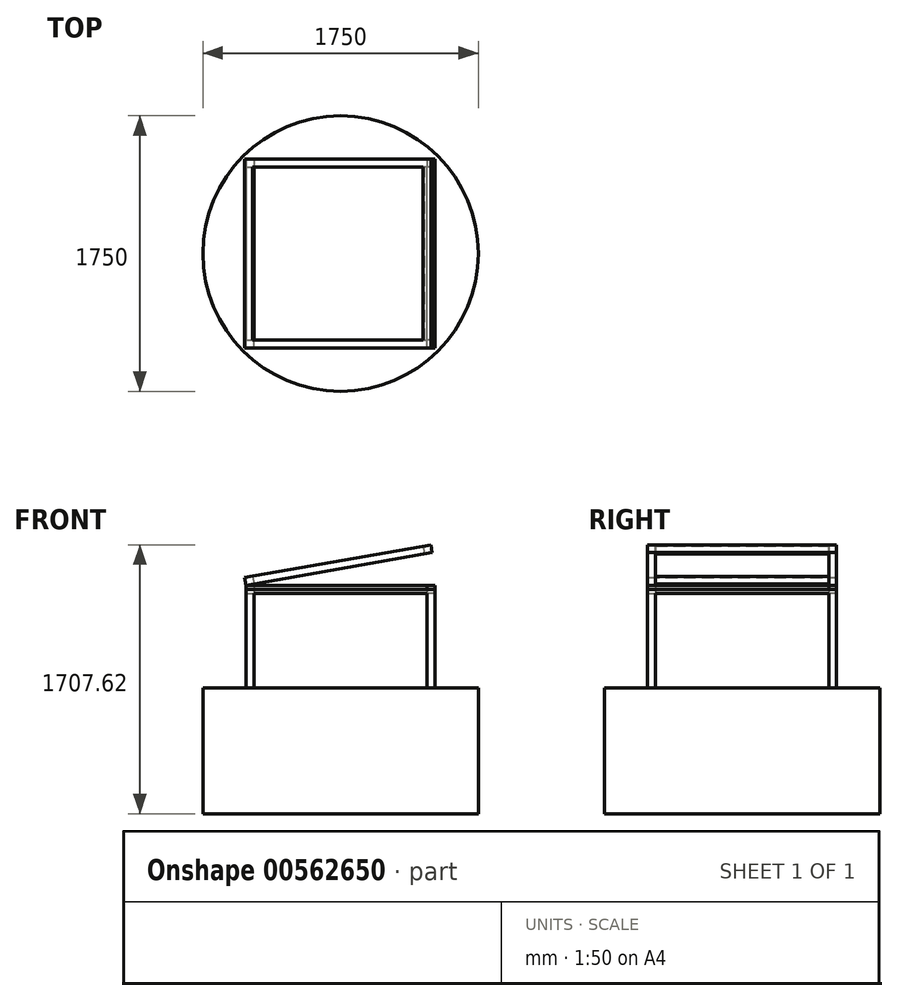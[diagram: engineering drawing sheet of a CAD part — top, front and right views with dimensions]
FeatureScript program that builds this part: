
annotation { "Feature Type Name" : "Feature", "Feature Type Description" : "" }
export const myFeature = defineFeature(function(context is Context, id is Id, definition is map)
    precondition{}
    {
        {
            var Q0;
            Q0=qCreatedBy(makeId("Top.planeOp"),FACE);
            var sketch = newSketch(context, id + "F0", { "sketchPlane" : qUnion([Q0])});
            skCircle(sketch, "E0", {"center": v(0, 0) * mm, "radius": 875 * mm});
            skSolve(sketch);
        }
        {
            var Q0;
            Q0=qSketchRegion(id+"F0",true);
            extrude(context, id + "F1", {"entities" : qUnion([Q0]), "oppositeDirection" : true, "depth" : 800 * mm});
        }
        {
            var Q0;
            Q0=qCreatedBy(makeId("Top.planeOp"),FACE);
            cPlane(context, id + "F2", {"entities" : qUnion([Q0]), "cplaneType" : CPlaneType.OFFSET, "offset" : 600 * mm, "width" : 150 * mm, "height" : 150 * mm});
        }
        {
            var Q0;
            Q0=qCreatedBy(id+"F2.planeOp",FACE);
            var sketch = newSketch(context, id + "F3", { "sketchPlane" : qUnion([Q0])});
            skLineSegment(sketch, "E1.bottom", {"start": v(600, -550) * mm, "end": v(550, -550) * mm});
            skLineSegment(sketch, "E1.top", {"start": v(600, 600) * mm, "end": v(550, 600) * mm});
            skLineSegment(sketch, "E1.left", {"start": v(600, -550) * mm, "end": v(600, 600) * mm});
            skLineSegment(sketch, "E1.right", {"start": v(550, -550) * mm, "end": v(550, 600) * mm});
            skSolve(sketch);
        }
        {
            var Q0;
            Q0=makeQuery(id+"F3.imprint","IMPRINT",FACE,{"disambiguationData":[TD([[makeQuery(id+"F3.imprint","IMPRINT",EDGE,{"derivedFrom":sQuery(id+"F3.wireOp",EDGE,"E1.bottom")}),-1.0]])]});
            extrude(context, id + "F4", {"entities" : qUnion([Q0]), "depth" : 25 * mm});
        }
        {
            var Q0;
            Q0=makeQuery(id+"F4.opExtrude","SWEPT_BODY",BODY,{"disambiguationData":[OSD([sQuery(id+"F3.wireOp",EDGE,"E1.bottom"),sQuery(id+"F3.wireOp",EDGE,"E1.top"),sQuery(id+"F3.wireOp",EDGE,"E1.left"),sQuery(id+"F3.wireOp",EDGE,"E1.right")])]});
            var Q1;
            Q1=makeQuery(id+"F1.opExtrude","SWEPT_FACE",FACE,{"disambiguationData":[OSD([sQuery(id+"F0.wireOp",EDGE,"E0")])]});
            circularPattern(context, id + "F5", {"entities" : qUnion([Q0]), "axis" : qUnion([Q1]), "angle" : 90 * degree, "instanceCount" : 4, "computeTransformsWithoutBuiltin" : true});
        }
        {
            var Q0;
            Q0=makeQuery(id+"F4.opExtrude","CAP_FACE",FACE,{"disambiguationData":[OSD([sQuery(id+"F3.wireOp",EDGE,"E1.bottom"),sQuery(id+"F3.wireOp",EDGE,"E1.top"),sQuery(id+"F3.wireOp",EDGE,"E1.left"),sQuery(id+"F3.wireOp",EDGE,"E1.right")])],"isStart":false});
            var sketch = newSketch(context, id + "F6", { "sketchPlane" : qUnion([Q0])});
            skLineSegment(sketch, "E2.bottom", {"start": v(-600, -600) * mm, "end": v(550, -600) * mm});
            skLineSegment(sketch, "E2.top", {"start": v(-600, -550) * mm, "end": v(550, -550) * mm});
            skLineSegment(sketch, "E2.left", {"start": v(-600, -600) * mm, "end": v(-600, -550) * mm});
            skLineSegment(sketch, "E2.right", {"start": v(550, -600) * mm, "end": v(550, -550) * mm});
            skSolve(sketch);
        }
        {
            var Q0;
            Q0=qSketchRegion(id+"F6",true);
            extrude(context, id + "F7", {"entities" : qUnion([Q0]), "depth" : 25 * mm});
        }
        {
            var Q0;
            Q0=makeQuery(id+"F7.opExtrude","SWEPT_BODY",BODY,{"disambiguationData":[OSD([sQuery(id+"F6.wireOp",EDGE,"E2.bottom"),sQuery(id+"F6.wireOp",EDGE,"E2.top"),sQuery(id+"F6.wireOp",EDGE,"E2.left"),sQuery(id+"F6.wireOp",EDGE,"E2.right")])]});
            var Q1;
            Q1=makeQuery(id+"F1.opExtrude","SWEPT_FACE",FACE,{"disambiguationData":[OSD([sQuery(id+"F0.wireOp",EDGE,"E0")])]});
            circularPattern(context, id + "F8", {"entities" : qUnion([Q0]), "axis" : qUnion([Q1]), "angle" : 90 * degree, "instanceCount" : 4, "computeTransformsWithoutBuiltin" : true});
        }
        {
            var Q0;
            Q0=qCreatedBy(id+"F2.planeOp",FACE);
            var sketch = newSketch(context, id + "F9", { "sketchPlane" : qUnion([Q0])});
            skLineSegment(sketch, "E3.bottom", {"start": v(600, -600) * mm, "end": v(550, -600) * mm});
            skLineSegment(sketch, "E3.top", {"start": v(600, -550) * mm, "end": v(550, -550) * mm});
            skLineSegment(sketch, "E3.left", {"start": v(600, -600) * mm, "end": v(600, -550) * mm});
            skLineSegment(sketch, "E3.right", {"start": v(550, -600) * mm, "end": v(550, -550) * mm});
            skSolve(sketch);
        }
        {
            var Q0;
            Q0=qSketchRegion(id+"F9",true);
            extrude(context, id + "F10", {"entities" : qUnion([Q0]), "oppositeDirection" : true, "depth" : 800 * mm});
        }
        {
            var Q0;
            Q0=makeQuery(id+"F10.opExtrude","SWEPT_BODY",BODY,{"disambiguationData":[OSD([sQuery(id+"F9.wireOp",EDGE,"E3.bottom"),sQuery(id+"F9.wireOp",EDGE,"E3.top"),sQuery(id+"F9.wireOp",EDGE,"E3.left"),sQuery(id+"F9.wireOp",EDGE,"E3.right")])]});
            var Q1;
            Q1=makeQuery(id+"F1.opExtrude","SWEPT_FACE",FACE,{"disambiguationData":[OSD([sQuery(id+"F0.wireOp",EDGE,"E0")])]});
            circularPattern(context, id + "F11", {"operationType" : NewBodyOperationType.ADD, "entities" : qUnion([Q0]), "axis" : qUnion([Q1]), "angle" : 90 * degree, "instanceCount" : 4, "computeTransformsWithoutBuiltin" : true});
        }
        {
            var Q0;
            Q0=makeQuery(id+"F8.opPattern","COPY",EDGE,{"derivedFrom":makeQuery(id+"F7.opExtrude","CAP_EDGE",EDGE,{"disambiguationData":[OSD([sQuery(id+"F6.wireOp",EDGE,"E2.bottom")])],"isStart":false}),"instanceName":"3"});
            cPlane(context, id + "F12", {"entities" : qUnion([Q0]), "cplaneType" : CPlaneType.LINE_ANGLE, "offset" : 150 * mm, "angle" : 10 * degree, "width" : 150 * mm, "height" : 150 * mm});
        }
        {
            var Q0;
            Q0=qCreatedBy(id+"F12.planeOp",FACE);
            var sketch = newSketch(context, id + "F13", { "sketchPlane" : qUnion([Q0])});
            skLineSegment(sketch, "E4.bottom", {"start": v(-478.01, 600) * mm, "end": v(721.99, 600) * mm});
            skLineSegment(sketch, "E4.top", {"start": v(-478.01, -600) * mm, "end": v(721.99, -600) * mm});
            skLineSegment(sketch, "E4.left", {"start": v(-478.01, 600) * mm, "end": v(-478.01, -600) * mm});
            skLineSegment(sketch, "E4.right", {"start": v(721.99, 600) * mm, "end": v(721.99, -600) * mm});
            skLineSegment(sketch, "E5.bottom", {"start": v(-428.01, 550) * mm, "end": v(671.99, 550) * mm});
            skLineSegment(sketch, "E5.top", {"start": v(-428.01, -550) * mm, "end": v(671.99, -550) * mm});
            skLineSegment(sketch, "E5.left", {"start": v(-428.01, 550) * mm, "end": v(-428.01, -550) * mm});
            skLineSegment(sketch, "E5.right", {"start": v(671.99, 550) * mm, "end": v(671.99, -550) * mm});
            skSolve(sketch);
        }
        {
            var Q0;
            Q0=qSketchRegion(id+"F13",true);
            extrude(context, id + "F14", {"entities" : qUnion([Q0]), "oppositeDirection" : true, "depth" : 50 * mm});
        }
    });
